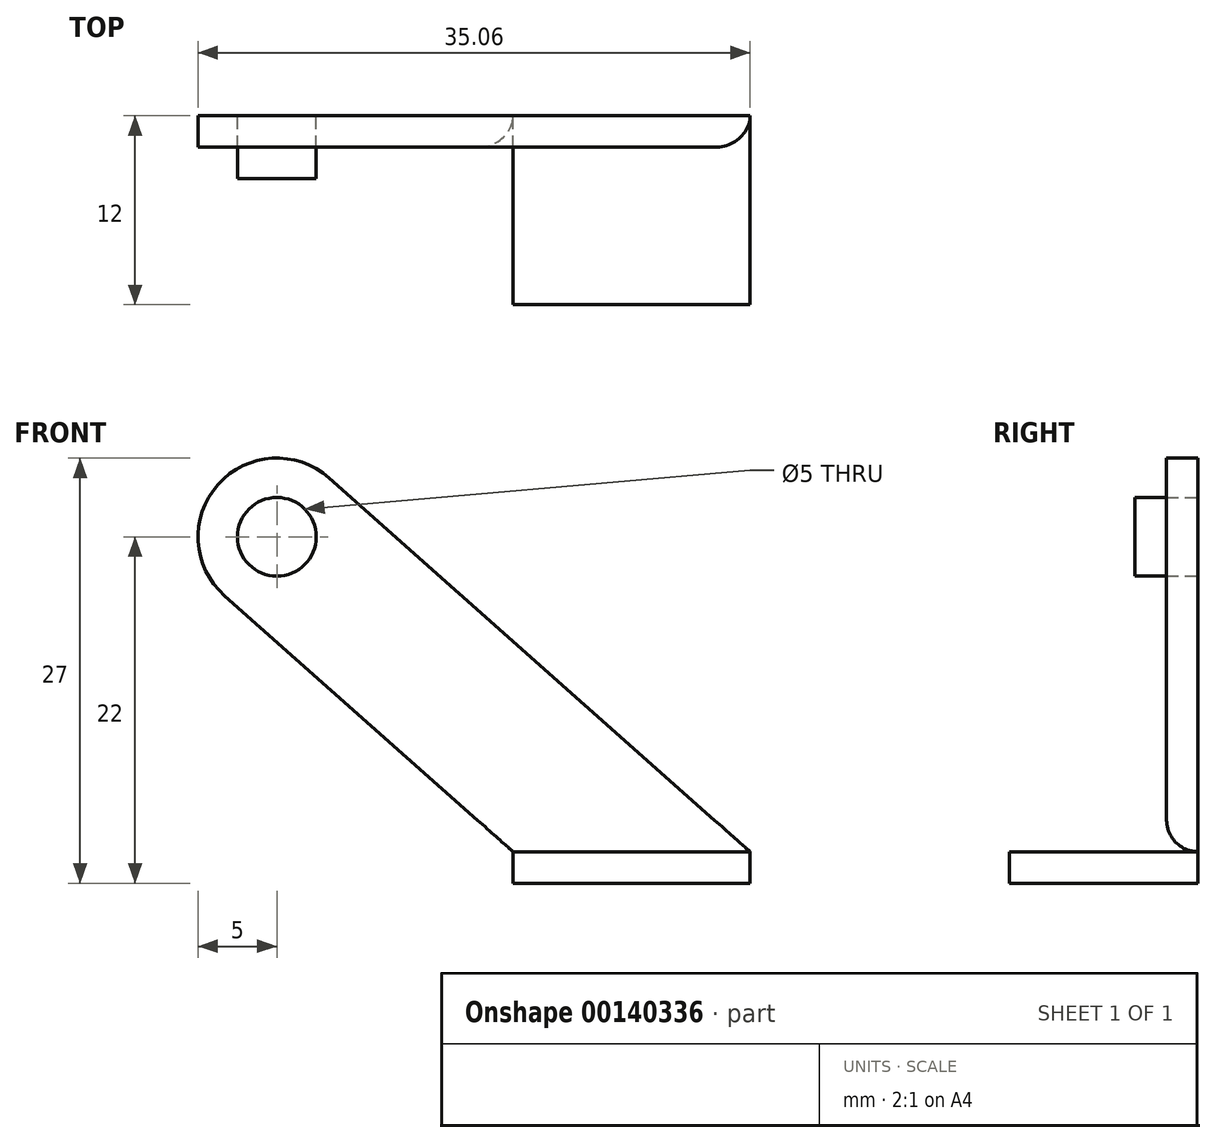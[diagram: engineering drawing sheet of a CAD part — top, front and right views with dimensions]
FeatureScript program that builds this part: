
annotation { "Feature Type Name" : "Feature", "Feature Type Description" : "" }
export const myFeature = defineFeature(function(context is Context, id is Id, definition is map)
    precondition{}
    {
        {
            var Q0;
            Q0=qCreatedBy(makeId("Front.planeOp"),FACE);
            var sketch = newSketch(context, id + "F0", { "sketchPlane" : qUnion([Q0])});
            skPoint(sketch, "E0.middle", {"position": v(0, 0) * mm});
            skCircle(sketch, "E1", {"center": v(0, 0) * mm, "radius": 2.5 * mm});
            skArc(sketch, "E2", {"start": v(3.32, 3.74) * mm, "mid": v(-3.74, 3.32) * mm, "end": v(-3.32, -3.74) * mm});
            skLineSegment(sketch, "E3", {"start": v(15, -20) * mm, "end": v(-3.32, -3.74) * mm});
            skLineSegment(sketch, "E4", {"start": v(3.32, 3.74) * mm, "end": v(30.06, -20) * mm});
            skLineSegment(sketch, "E5", {"start": v(15, -20) * mm, "end": v(30.06, -20) * mm});
            skPoint(sketch, "E0.top.start.orphan", {"position": v(5, 20) * mm});
            skPoint(sketch, "E6.orphan", {"position": v(-5, 20) * mm});
            skPoint(sketch, "E0.bottom.end.orphan", {"position": v(-5, -20) * mm});
            skPoint(sketch, "E7.start.orphan", {"position": v(5, -20) * mm});
            skLineSegment(sketch, "E8", {"start": v(15, -20) * mm, "end": v(15, -22) * mm});
            skLineSegment(sketch, "E9", {"start": v(15, -22) * mm, "end": v(30.06, -22) * mm});
            skLineSegment(sketch, "E10", {"start": v(30.06, -22) * mm, "end": v(30.06, -20) * mm});
            skSolve(sketch);
        }
        {
            var Q0;
            Q0=makeQuery(id+"F0.imprint","IMPRINT",FACE,{"disambiguationData":[TD([[makeQuery(id+"F0.imprint","IMPRINT",EDGE,{"derivedFrom":sQuery(id+"F0.wireOp",EDGE,"E1")}),-1.0]])]});
            extrude(context, id + "F1", {"entities" : qUnion([Q0]), "oppositeDirection" : true, "depth" : 2 * mm});
        }
        {
            var Q0;
            {var subQ1=sQuery(id+"F0.wireOp",EDGE,"E8");Q0=makeQuery(id+"F0.imprint","IMPRINT",FACE,{"disambiguationData":[TD([[makeQuery(id+"F0.imprint","IMPRINT",EDGE,{"derivedFrom":subQ1}),1.0]])]});}
            extrude(context, id + "F2", {"entities" : qUnion([Q0]), "depth" : 10 * mm, "hasSecondDirection" : true, "secondDirectionOppositeDirection" : true, "secondDirectionDepth" : 2 * mm});
        }
        {
            var Q0;
            Q0=makeQuery(id+"F0.imprint","IMPRINT",FACE,{"disambiguationData":[TD([[makeQuery(id+"F0.imprint","IMPRINT",EDGE,{"derivedFrom":sQuery(id+"F0.wireOp",EDGE,"E1")}),1.0]])]});
            extrude(context, id + "F3", {"entities" : qUnion([Q0]), "depth" : 2 * mm, "hasSecondDirection" : true, "secondDirectionOppositeDirection" : true, "secondDirectionDepth" : 2 * mm});
        }
        {
            var Q0;
            Q0=makeQuery(id+"F1.opExtrude","CAP_EDGE",EDGE,{"disambiguationData":[OSD([sQuery(id+"F0.wireOp",EDGE,"E5")])],"isStart":true});
            fillet(context, id + "F4", {"entities" : qUnion([Q0]), "radius" : 2 * mm, "tangentPropagation" : true, "allowEdgeOverflow" : false});
        }
    });
